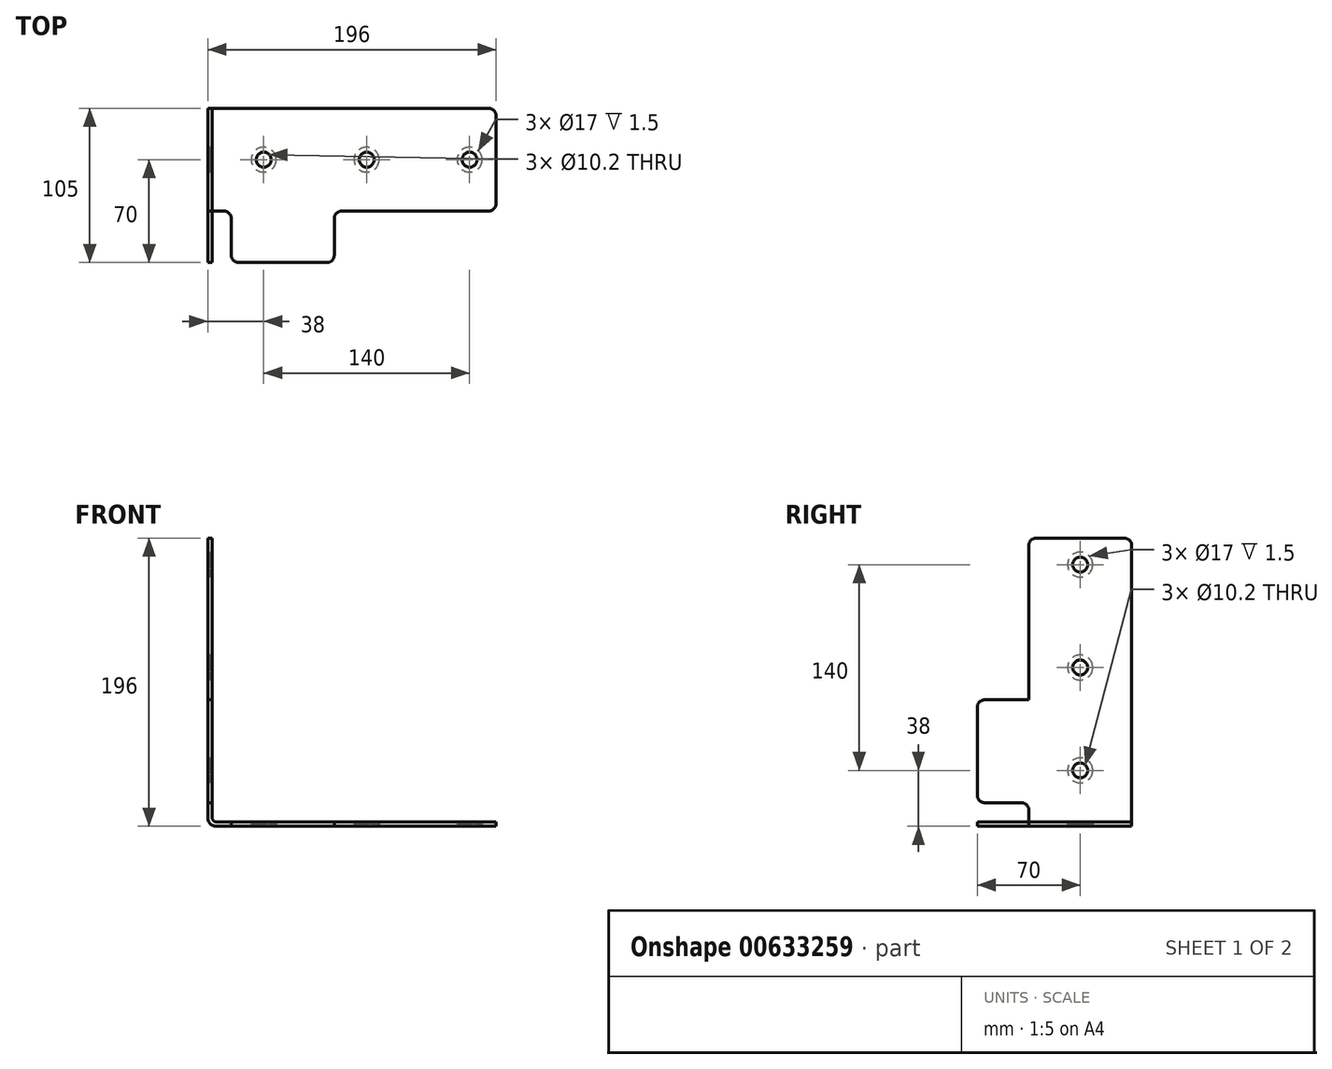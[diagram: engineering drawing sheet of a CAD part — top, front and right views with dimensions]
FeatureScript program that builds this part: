
annotation { "Feature Type Name" : "Feature", "Feature Type Description" : "" }
export const myFeature = defineFeature(function(context is Context, id is Id, definition is map)
    precondition{}
    {
        {
            var Q0;
            Q0=qCreatedBy(makeId("Right.planeOp"),FACE);
            var Q1;
            Q1=qCreatedBy(makeId("Top.planeOp"),FACE);
            cPlane(context, id + "F0", {"entities" : qUnion([Q0, Q1]), "cplaneType" : CPlaneType.MID_PLANE, "offset" : 25 * mm, "width" : 150 * mm, "height" : 150 * mm});
        }
        {
            var Q0;
            Q0=qCreatedBy(makeId("Front.planeOp"),FACE);
            var sketch = newSketch(context, id + "F1", { "sketchPlane" : qUnion([Q0])});
            skLineSegment(sketch, "E0", {"start": v(0, 196) * mm, "end": v(0, 0) * mm});
            skLineSegment(sketch, "E1", {"start": v(0, 0) * mm, "end": v(196, 0) * mm});
            skLineSegment(sketch, "E2.0", {"start": v(3, 3) * mm, "end": v(196, 3) * mm});
            skLineSegment(sketch, "E2.1", {"start": v(3, 196) * mm, "end": v(3, 3) * mm});
            skLineSegment(sketch, "E3", {"start": v(196, 0) * mm, "end": v(196, 3) * mm});
            skLineSegment(sketch, "E4", {"start": v(0, 196) * mm, "end": v(3, 196) * mm});
            skSolve(sketch);
        }
        {
            var Q0;
            Q0=qSketchRegion(id+"F1",true);
            extrude(context, id + "F2", {"entities" : qUnion([Q0]), "oppositeDirection" : true, "depth" : 70 * mm});
        }
        {
            var Q0;
            Q0=makeQuery(id+"F2.opExtrude","SWEPT_EDGE",EDGE,{"disambiguationData":[OSD([sQuery(id+"F1.wireOp",EDGE,"E0"),sQuery(id+"F1.wireOp",EDGE,"E1")])]});
            fillet(context, id + "F3", {"entities" : qUnion([Q0]), "radius" : 5.6 * mm, "tangentPropagation" : true, "allowEdgeOverflow" : false});
        }
        {
            var Q0;
            Q0=makeQuery(id+"F2.opExtrude","SWEPT_EDGE",EDGE,{"disambiguationData":[OSD([sQuery(id+"F1.wireOp",EDGE,"E2.0"),sQuery(id+"F1.wireOp",EDGE,"E2.1")])]});
            fillet(context, id + "F4", {"entities" : qUnion([Q0]), "radius" : 2.6 * mm, "tangentPropagation" : true, "allowEdgeOverflow" : false});
        }
        {
            var Q0;
            Q0=makeQuery(id+"F2.opExtrude","CAP_FACE",FACE,{"disambiguationData":[OSD([sQuery(id+"F1.wireOp",EDGE,"E0"),sQuery(id+"F1.wireOp",EDGE,"E1"),sQuery(id+"F1.wireOp",EDGE,"E2.0"),sQuery(id+"F1.wireOp",EDGE,"E2.1"),sQuery(id+"F1.wireOp",EDGE,"E3"),sQuery(id+"F1.wireOp",EDGE,"E4")])],"isStart":true});
            var sketch = newSketch(context, id + "F5", { "sketchPlane" : qUnion([Q0])});
            skLineSegment(sketch, "E5", {"start": v(16, 3) * mm, "end": v(86, 3) * mm});
            skLineSegment(sketch, "E6", {"start": v(86, 3) * mm, "end": v(86, 0) * mm});
            skLineSegment(sketch, "E7", {"start": v(86, 0) * mm, "end": v(16, 0) * mm});
            skLineSegment(sketch, "E8", {"start": v(16, 3) * mm, "end": v(16, 0) * mm});
            skLineSegment(sketch, "E9.MirrorCS", {"start": v(3, 16) * mm, "end": v(0, 16) * mm});
            skLineSegment(sketch, "E10.MirrorCS", {"start": v(3, 16) * mm, "end": v(3, 86) * mm});
            skLineSegment(sketch, "E11.MirrorCS", {"start": v(0, 86) * mm, "end": v(0, 16) * mm});
            skLineSegment(sketch, "E12.MirrorCS", {"start": v(3, 86) * mm, "end": v(0, 86) * mm});
            skSolve(sketch);
        }
        {
            var Q0;
            Q0=qSketchRegion(id+"F5",true);
            extrude(context, id + "F6", {"entities" : qUnion([Q0]), "operationType" : NewBodyOperationType.ADD, "depth" : 35 * mm});
        }
        {
            var Q0;
            Q0=makeQuery(id+"F6.opExtrude","CAP_EDGE",EDGE,{"disambiguationData":[OSD([sQuery(id+"F5.wireOp",EDGE,"E8")])],"isStart":true});
            var Q1;
            Q1=makeQuery(id+"F6.opExtrude","CAP_EDGE",EDGE,{"disambiguationData":[OSD([sQuery(id+"F5.wireOp",EDGE,"E8")])],"isStart":false});
            var Q2;
            Q2=makeQuery(id+"F6.opExtrude","CAP_EDGE",EDGE,{"disambiguationData":[OSD([sQuery(id+"F5.wireOp",EDGE,"E6")])],"isStart":false});
            var Q3;
            Q3=makeQuery(id+"F6.opExtrude","CAP_EDGE",EDGE,{"disambiguationData":[OSD([sQuery(id+"F5.wireOp",EDGE,"E6")])],"isStart":true});
            var Q4;
            Q4=makeQuery(id+"F6.opExtrude","CAP_EDGE",EDGE,{"disambiguationData":[OSD([sQuery(id+"F5.wireOp",EDGE,"E9.MirrorCS")])],"isStart":false});
            var Q5;
            Q5=makeQuery(id+"F6.opExtrude","CAP_EDGE",EDGE,{"disambiguationData":[OSD([sQuery(id+"F5.wireOp",EDGE,"E12.MirrorCS")])],"isStart":false});
            var Q6;
            Q6=makeQuery(id+"F6.opExtrude","CAP_EDGE",EDGE,{"disambiguationData":[OSD([sQuery(id+"F5.wireOp",EDGE,"E9.MirrorCS")])],"isStart":true});
            var Q7;
            Q7=makeQuery(id+"F6.opExtrude","CAP_EDGE",EDGE,{"disambiguationData":[OSD([sQuery(id+"F5.wireOp",EDGE,"E12.MirrorCS")])],"isStart":true});
            var Q8;
            Q8=makeQuery(id+"F2.opExtrude","CAP_EDGE",EDGE,{"disambiguationData":[OSD([sQuery(id+"F1.wireOp",EDGE,"E4")])],"isStart":true});
            var Q9;
            Q9=makeQuery(id+"F2.opExtrude","CAP_EDGE",EDGE,{"disambiguationData":[OSD([sQuery(id+"F1.wireOp",EDGE,"E4")])],"isStart":false});
            var Q10;
            Q10=makeQuery(id+"F2.opExtrude","CAP_EDGE",EDGE,{"disambiguationData":[OSD([sQuery(id+"F1.wireOp",EDGE,"E3")])],"isStart":false});
            var Q11;
            Q11=makeQuery(id+"F2.opExtrude","CAP_EDGE",EDGE,{"disambiguationData":[OSD([sQuery(id+"F1.wireOp",EDGE,"E3")])],"isStart":true});
            fillet(context, id + "F7", {"entities" : qUnion([Q0, Q1, Q2, Q3, Q4, Q5, Q6, Q7, Q8, Q9, Q10, Q11]), "radius" : 5 * mm, "tangentPropagation" : true, "allowEdgeOverflow" : false});
        }
        {
            var Q0;
            Q0=makeQuery(id+"F6.boolean.opBoolean","MERGE",FACE,{"derivedFrom":[makeQuery(id+"F2.opExtrude","SWEPT_FACE",FACE,{"disambiguationData":[OSD([sQuery(id+"F1.wireOp",EDGE,"E1")])]}),makeQuery(id+"F6.opExtrude","SWEPT_FACE",FACE,{"disambiguationData":[OSD([sQuery(id+"F5.wireOp",EDGE,"E7")])]})]});
            var sketch = newSketch(context, id + "F8", { "sketchPlane" : qUnion([Q0])});
            skPoint(sketch, "E13", {"position": v(38, -35) * mm});
            skPoint(sketch, "E14", {"position": v(108, -35) * mm});
            skPoint(sketch, "E15", {"position": v(178, -35) * mm});
            skSolve(sketch);
        }
        {
            var Q0;
            Q0=makeQuery(id+"F6.boolean.opBoolean","MERGE",FACE,{"derivedFrom":[makeQuery(id+"F2.opExtrude","SWEPT_FACE",FACE,{"disambiguationData":[OSD([sQuery(id+"F1.wireOp",EDGE,"E0")])]}),makeQuery(id+"F6.opExtrude","SWEPT_FACE",FACE,{"disambiguationData":[OSD([sQuery(id+"F5.wireOp",EDGE,"E11.MirrorCS")])]})]});
            var sketch = newSketch(context, id + "F9", { "sketchPlane" : qUnion([Q0])});
            skPoint(sketch, "E16", {"position": v(-35, 178) * mm});
            skPoint(sketch, "E17", {"position": v(-35, 108) * mm});
            skPoint(sketch, "E18", {"position": v(-35, 38) * mm});
            skSolve(sketch);
        }
        {
            var Q0;
            Q0=sQuery(id+"F8.wireOp",VERTEX,"E13");
            var Q1;
            Q1=sQuery(id+"F8.wireOp",VERTEX,"E14");
            var Q2;
            Q2=sQuery(id+"F8.wireOp",VERTEX,"E15");
            var Q3;
            Q3=sQuery(id+"F9.wireOp",VERTEX,"E16");
            var Q4;
            Q4=sQuery(id+"F9.wireOp",VERTEX,"E17");
            var Q5;
            Q5=sQuery(id+"F9.wireOp",VERTEX,"E18");
            var Q6;
            Q6=makeQuery(id+"F2.opExtrude","SWEPT_BODY",BODY,{"disambiguationData":[OSD([sQuery(id+"F1.wireOp",EDGE,"E0"),sQuery(id+"F1.wireOp",EDGE,"E1"),sQuery(id+"F1.wireOp",EDGE,"E2.0"),sQuery(id+"F1.wireOp",EDGE,"E2.1"),sQuery(id+"F1.wireOp",EDGE,"E3"),sQuery(id+"F1.wireOp",EDGE,"E4")])]});
            hole(context, id + "F10", {"style" : HoleStyle.C_BORE, "endStyle" : HoleEndStyle.THROUGH, "holeDiameter" : 10.2 * mm, "cBoreDiameter" : 17 * mm, "cBoreDepth" : 1.5 * mm, "locations" : qUnion([Q0, Q1, Q2, Q3, Q4, Q5]), "scope" : qUnion([Q6]), "isTappedThrough" : true});
        }
    });
